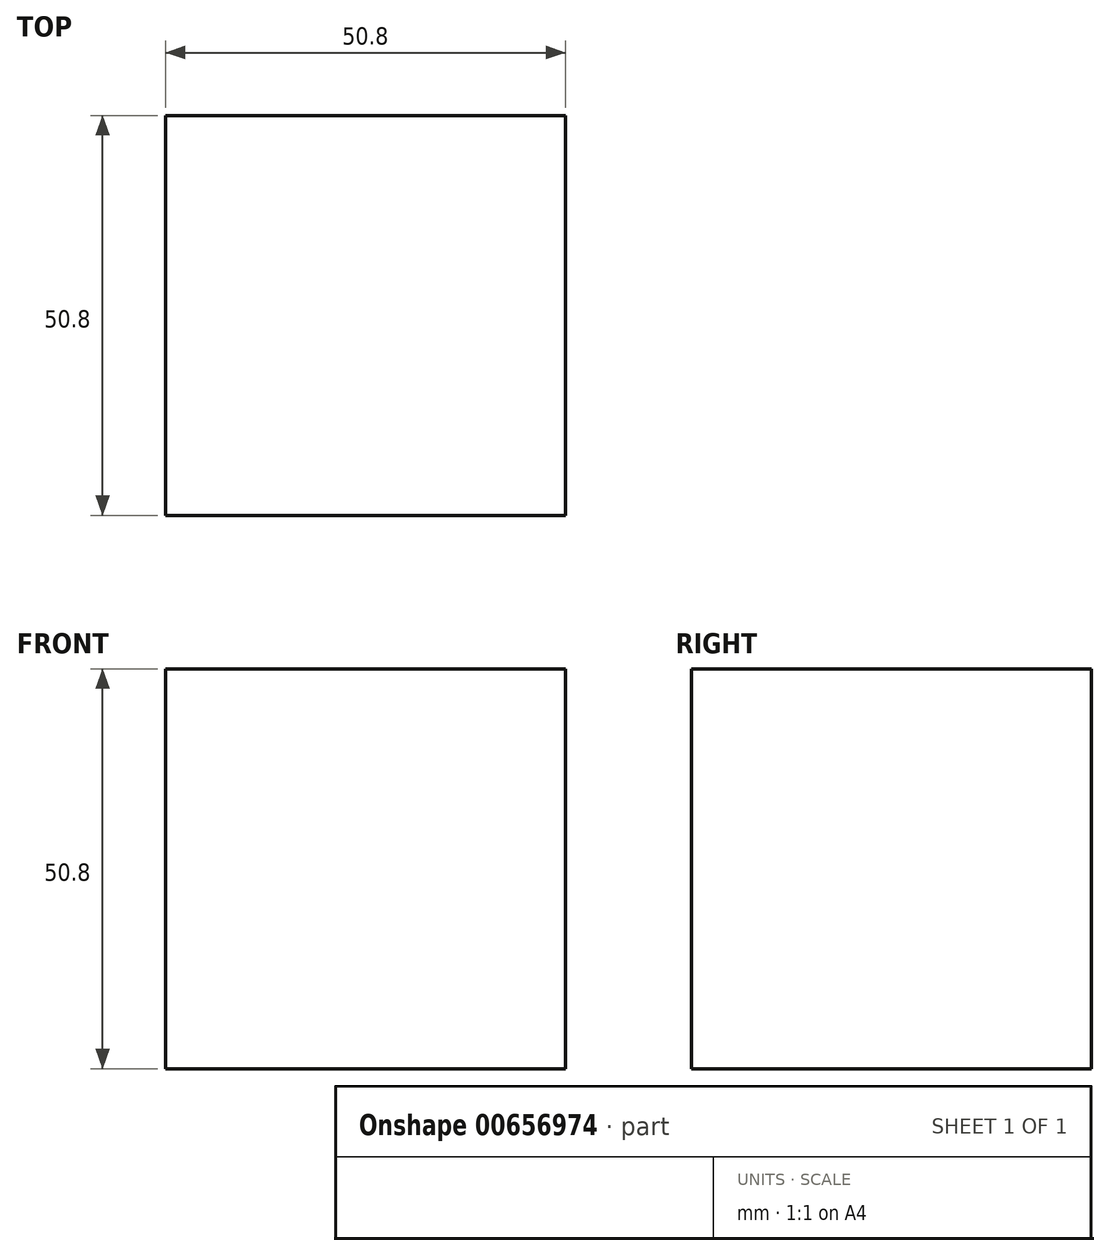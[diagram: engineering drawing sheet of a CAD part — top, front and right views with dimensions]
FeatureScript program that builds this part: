
annotation { "Feature Type Name" : "Feature", "Feature Type Description" : "" }
export const myFeature = defineFeature(function(context is Context, id is Id, definition is map)
    precondition{}
    {
        {
            var Q0;
            Q0=qCreatedBy(makeId("Front.planeOp"),FACE);
            var sketch = newSketch(context, id + "F0", { "sketchPlane" : qUnion([Q0])});
            skLineSegment(sketch, "E0", {"start": v(-60.21, -27.23) * mm, "end": v(-9.41, -27.23) * mm});
            skLineSegment(sketch, "E1", {"start": v(-9.41, -27.23) * mm, "end": v(-9.41, 23.57) * mm});
            skLineSegment(sketch, "E2", {"start": v(-9.41, 23.57) * mm, "end": v(-60.21, 23.57) * mm});
            skLineSegment(sketch, "E3", {"start": v(-60.21, 23.57) * mm, "end": v(-60.21, -27.23) * mm});
            skSolve(sketch);
        }
        {
            var Q0;
            Q0=makeQuery(id+"F0.imprint","IMPRINT",FACE,{"disambiguationData":[TD([[makeQuery(id+"F0.imprint","IMPRINT",EDGE,{"derivedFrom":sQuery(id+"F0.wireOp",EDGE,"E0")}),1.0]])]});
            extrude(context, id + "F1", {"entities" : qUnion([Q0]), "depth" : 50.8 * mm, "offsetDistance" : 25.4 * mm});
        }
    });
